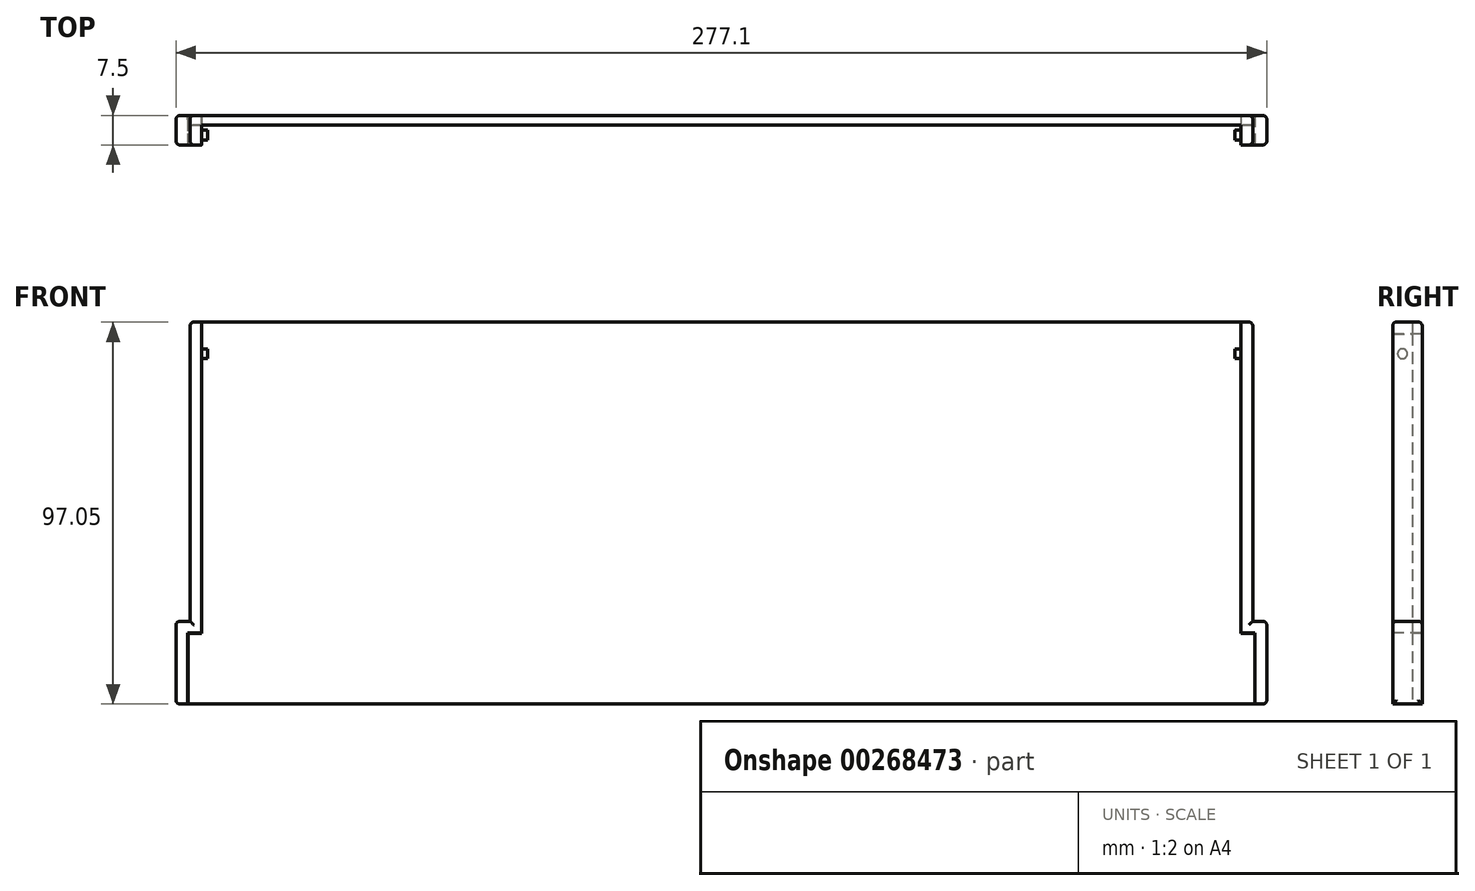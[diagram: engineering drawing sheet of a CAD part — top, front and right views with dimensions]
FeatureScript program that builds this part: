
annotation { "Feature Type Name" : "Feature", "Feature Type Description" : "" }
export const myFeature = defineFeature(function(context is Context, id is Id, definition is map)
    precondition{}
    {
        {
            var Q0;
            Q0=qCreatedBy(makeId("Front.planeOp"),FACE);
            var sketch = newSketch(context, id + "F0", { "sketchPlane" : qUnion([Q0])});
            skLineSegment(sketch, "E0", {"start": v(0, 0) * mm, "end": v(-135.5, 0) * mm});
            skLineSegment(sketch, "E1", {"start": v(-135.5, 0) * mm, "end": v(-135.5, 18) * mm});
            skLineSegment(sketch, "E2", {"start": v(-135.5, 18) * mm, "end": v(-132, 18) * mm});
            skLineSegment(sketch, "E3", {"start": v(-132, 18) * mm, "end": v(-132, 160) * mm});
            skLineSegment(sketch, "E4", {"start": v(-132, 160) * mm, "end": v(132, 160) * mm});
            skLineSegment(sketch, "E5", {"start": v(132, 160) * mm, "end": v(132, 18) * mm});
            skLineSegment(sketch, "E6", {"start": v(132, 18) * mm, "end": v(135.5, 18) * mm});
            skLineSegment(sketch, "E7", {"start": v(135.5, 18) * mm, "end": v(135.5, 0) * mm});
            skLineSegment(sketch, "E8", {"start": v(135.5, 0) * mm, "end": v(0, 0) * mm});
            skSolve(sketch);
        }
        {
            var Q0;
            Q0=makeQuery(id+"F0.imprint","IMPRINT",FACE,{"disambiguationData":[TD([[makeQuery(id+"F0.imprint","IMPRINT",EDGE,{"derivedFrom":sQuery(id+"F0.wireOp",EDGE,"E0")}),-1.0]])]});
            extrude(context, id + "F1", {"entities" : qUnion([Q0]), "oppositeDirection" : true, "depth" : 5 * mm, "offsetDistance" : 25 * mm});
        }
        {
            var Q0;
            Q0=makeQuery(id+"F1.opExtrude","CAP_FACE",FACE,{"disambiguationData":[OSD([sQuery(id+"F0.wireOp",EDGE,"E0"),sQuery(id+"F0.wireOp",EDGE,"E1"),sQuery(id+"F0.wireOp",EDGE,"E2"),sQuery(id+"F0.wireOp",EDGE,"E3"),sQuery(id+"F0.wireOp",EDGE,"E4"),sQuery(id+"F0.wireOp",EDGE,"E5"),sQuery(id+"F0.wireOp",EDGE,"E6"),sQuery(id+"F0.wireOp",EDGE,"E7"),sQuery(id+"F0.wireOp",EDGE,"E8")])],"isStart":true});
            var sketch = newSketch(context, id + "F2", { "sketchPlane" : qUnion([Q0])});
            skLineSegment(sketch, "E9", {"start": v(-135.55, 0) * mm, "end": v(-135.55, 18.05) * mm});
            skLineSegment(sketch, "E10", {"start": v(-135.55, 18.05) * mm, "end": v(-132.05, 18.05) * mm});
            skLineSegment(sketch, "E11", {"start": v(-132.05, 18.05) * mm, "end": v(-132.05, 94.05) * mm});
            skLineSegment(sketch, "E12", {"start": v(-132.05, 94.05) * mm, "end": v(132.05, 94.05) * mm});
            skLineSegment(sketch, "E13", {"start": v(132.05, 94.05) * mm, "end": v(132.05, 18.05) * mm});
            skLineSegment(sketch, "E14", {"start": v(132.05, 18.05) * mm, "end": v(135.55, 18.05) * mm});
            skLineSegment(sketch, "E15", {"start": v(135.55, 18.05) * mm, "end": v(135.55, 0) * mm});
            skLineSegment(sketch, "E16", {"start": v(135.55, 0) * mm, "end": v(138.55, 0) * mm});
            skLineSegment(sketch, "E17", {"start": v(138.55, 0) * mm, "end": v(138.55, 21.05) * mm});
            skLineSegment(sketch, "E18", {"start": v(138.55, 21.05) * mm, "end": v(135, 21.05) * mm});
            skLineSegment(sketch, "E19", {"start": v(135, 21.05) * mm, "end": v(135, 97.05) * mm});
            skLineSegment(sketch, "E20", {"start": v(135, 97.05) * mm, "end": v(-135, 97.05) * mm});
            skLineSegment(sketch, "E21", {"start": v(-135, 97.05) * mm, "end": v(-135, 21.05) * mm});
            skLineSegment(sketch, "E22", {"start": v(-135, 21.05) * mm, "end": v(-138.55, 21.05) * mm});
            skLineSegment(sketch, "E23", {"start": v(-138.55, 21.05) * mm, "end": v(-138.55, 0) * mm});
            skLineSegment(sketch, "E24", {"start": v(-138.55, 0) * mm, "end": v(-135.55, 0) * mm});
            skLineSegment(sketch, "E25.bottom", {"start": v(138.55, 0) * mm, "end": v(135.55, 0) * mm});
            skLineSegment(sketch, "E25.top", {"start": v(138.55, 0) * mm, "end": v(135.55, 0) * mm});
            skLineSegment(sketch, "E25.left", {"start": v(138.55, 0) * mm, "end": v(138.55, 0) * mm});
            skLineSegment(sketch, "E25.right", {"start": v(135.55, 0) * mm, "end": v(135.55, 0) * mm});
            skLineSegment(sketch, "E26.left", {"start": v(-138.55, 0) * mm, "end": v(-138.55, 0) * mm});
            skLineSegment(sketch, "E26.right", {"start": v(-135.55, 0) * mm, "end": v(-135.55, 0) * mm});
            skSolve(sketch);
        }
        {
            var Q0;
            Q0=makeQuery(id+"F1.opExtrude","SWEPT_FACE",FACE,{"disambiguationData":[OSD([sQuery(id+"F0.wireOp",EDGE,"E5")])]});
            var sketch = newSketch(context, id + "F3", { "sketchPlane" : qUnion([Q0])});
            skCircle(sketch, "E27", {"center": v(2.5, 89) * mm, "radius": 1.25 * mm});
            skPoint(sketch, "E27.centerSnap0", {"position": v(5, 89) * mm});
            skSolve(sketch);
        }
        {
            var Q0;
            Q0=makeQuery(id+"F1.opExtrude","SWEPT_FACE",FACE,{"disambiguationData":[OSD([sQuery(id+"F0.wireOp",EDGE,"E3")])]});
            var sketch = newSketch(context, id + "F4", { "sketchPlane" : qUnion([Q0])});
            skCircle(sketch, "E28", {"center": v(-2.5, 89) * mm, "radius": 1.25 * mm});
            skPoint(sketch, "E28.centerSnap0", {"position": v(-5, 89) * mm});
            skSolve(sketch);
        }
        {
            var Q0;
            Q0 = qSketchRegion(id + "F2", true);
            extrude(context, id + "F5", {"entities" : qUnion([Q0]), "operationType" : NewBodyOperationType.ADD, "oppositeDirection" : true, "depth" : 7.5 * mm, "offsetDistance" : 25 * mm});
        }
        {
            var Q0;
            {var subQ0=sQuery(id+"F0.wireOp",EDGE,"E3");var subQ1=sQuery(id+"F0.wireOp",EDGE,"E2");var subQ2=sQuery(id+"F0.wireOp",EDGE,"E1");var subQ3=sQuery(id+"F0.wireOp",EDGE,"E8");var subQ4=sQuery(id+"F0.wireOp",EDGE,"E0");var subQ5=sQuery(id+"F0.wireOp",EDGE,"E5");var subQ6=sQuery(id+"F0.wireOp",EDGE,"E6");var subQ7=sQuery(id+"F0.wireOp",EDGE,"E7");Q0=makeQuery(id+"F5.boolean.opBoolean","SPLIT",FACE,{"disambiguationData":[TD([makeQuery(id+"F1.opExtrude","SWEPT_FACE",FACE,{"disambiguationData":[OSD([subQ2])]})])],"derivedFrom":makeQuery(id+"F1.opExtrude","CAP_FACE",FACE,{"disambiguationData":[OSD([subQ4,subQ2,subQ1,subQ0,sQuery(id+"F0.wireOp",EDGE,"E4"),subQ5,subQ6,subQ7,subQ3])],"isStart":false})});}
            extrude(context, id + "F6", {"entities" : qUnion([Q0]), "operationType" : NewBodyOperationType.ADD, "depth" : 2.5 * mm, "offsetDistance" : 25 * mm});
        }
        {
            var Q0;
            Q0 = qSketchRegion(id + "F0", true);
            extrude(context, id + "F7", {"entities" : qUnion([Q0]), "operationType" : NewBodyOperationType.REMOVE, "oppositeDirection" : true, "depth" : 5 * mm, "offsetDistance" : 25 * mm});
        }
        {
            var Q0;
            Q0 = qSketchRegion(id + "F3", true);
            var Q1;
            Q1 = qSketchRegion(id + "F4", true);
            extrude(context, id + "F8", {"entities" : qUnion([Q0, Q1]), "operationType" : NewBodyOperationType.ADD, "depth" : 1.5 * mm, "offsetDistance" : 25 * mm});
        }
        {
            var Q0;
            Q0 = qSketchRegion(id + "F3", true);
            var Q1;
            Q1 = qSketchRegion(id + "F4", true);
            extrude(context, id + "F9", {"entities" : qUnion([Q0, Q1]), "operationType" : NewBodyOperationType.ADD, "oppositeDirection" : true, "depth" : 1.5 * mm, "offsetDistance" : 25 * mm});
        }
        {
            var Q0;
            Q0=makeQuery(id+"F5.opExtrude","CAP_EDGE",EDGE,{"disambiguationData":[OSD([sQuery(id+"F2.wireOp",EDGE,"E21")])],"isStart":true});
            var Q1;
            Q1=makeQuery(id+"F5.opExtrude","CAP_EDGE",EDGE,{"disambiguationData":[OSD([sQuery(id+"F2.wireOp",EDGE,"E21")])],"isStart":false});
            var Q2;
            Q2=makeQuery(id+"F5.opExtrude","CAP_EDGE",EDGE,{"disambiguationData":[OSD([sQuery(id+"F2.wireOp",EDGE,"E19")])],"isStart":false});
            var Q3;
            Q3=makeQuery(id+"F5.opExtrude","CAP_EDGE",EDGE,{"disambiguationData":[OSD([sQuery(id+"F2.wireOp",EDGE,"E19")])],"isStart":true});
            var Q4;
            Q4=makeQuery(id+"F5.opExtrude","SWEPT_EDGE",EDGE,{"disambiguationData":[OSD([sQuery(id+"F2.wireOp",EDGE,"E19"),sQuery(id+"F2.wireOp",EDGE,"E20")])]});
            var Q5;
            Q5=makeQuery(id+"F5.opExtrude","CAP_EDGE",EDGE,{"disambiguationData":[OSD([sQuery(id+"F2.wireOp",EDGE,"E20")])],"isStart":false});
            var Q6;
            Q6=makeQuery(id+"F5.opExtrude","SWEPT_EDGE",EDGE,{"disambiguationData":[OSD([sQuery(id+"F2.wireOp",EDGE,"E20"),sQuery(id+"F2.wireOp",EDGE,"E21")])]});
            var Q7;
            Q7=makeQuery(id+"F5.opExtrude","CAP_EDGE",EDGE,{"disambiguationData":[OSD([sQuery(id+"F2.wireOp",EDGE,"E22")])],"isStart":true});
            var Q8;
            Q8=makeQuery(id+"F5.opExtrude","CAP_EDGE",EDGE,{"disambiguationData":[OSD([sQuery(id+"F2.wireOp",EDGE,"E22")])],"isStart":false});
            var Q9;
            Q9=makeQuery(id+"F5.opExtrude","SWEPT_EDGE",EDGE,{"disambiguationData":[OSD([sQuery(id+"F2.wireOp",EDGE,"E22"),sQuery(id+"F2.wireOp",EDGE,"E23")])]});
            var Q10;
            Q10=makeQuery(id+"F5.opExtrude","CAP_EDGE",EDGE,{"disambiguationData":[OSD([sQuery(id+"F2.wireOp",EDGE,"E23")])],"isStart":true});
            var Q11;
            Q11=makeQuery(id+"F5.opExtrude","CAP_EDGE",EDGE,{"disambiguationData":[OSD([sQuery(id+"F2.wireOp",EDGE,"E23")])],"isStart":false});
            var Q12;
            Q12=makeQuery(id+"F5.opExtrude","SWEPT_EDGE",EDGE,{"disambiguationData":[OSD([sQuery(id+"F2.wireOp",EDGE,"E23"),sQuery(id+"F2.wireOp",EDGE,"E24")])]});
            var Q13;
            Q13=makeQuery(id+"F6.opExtrude","CAP_EDGE",EDGE,{"disambiguationData":[OSD([sQuery(id+"F0.wireOp",EDGE,"E0"),sQuery(id+"F0.wireOp",EDGE,"E8")])],"isStart":false});
            var Q14;
            Q14=makeQuery(id+"F5.opExtrude","CAP_EDGE",EDGE,{"disambiguationData":[OSD([sQuery(id+"F2.wireOp",EDGE,"E24")])],"isStart":false});
            var Q15;
            Q15=makeQuery(id+"F5.opExtrude","CAP_EDGE",EDGE,{"disambiguationData":[OSD([sQuery(id+"F2.wireOp",EDGE,"E25.top")])],"isStart":false});
            var Q16;
            Q16=makeQuery(id+"F5.opExtrude","CAP_EDGE",EDGE,{"disambiguationData":[OSD([sQuery(id+"F2.wireOp",EDGE,"E17")])],"isStart":false});
            var Q17;
            Q17=makeQuery(id+"F5.opExtrude","SWEPT_EDGE",EDGE,{"disambiguationData":[OSD([sQuery(id+"F2.wireOp",EDGE,"E17"),sQuery(id+"F2.wireOp",EDGE,"E25.top")])]});
            var Q18;
            Q18=makeQuery(id+"F5.opExtrude","CAP_EDGE",EDGE,{"disambiguationData":[OSD([sQuery(id+"F2.wireOp",EDGE,"E17")])],"isStart":true});
            var Q19;
            Q19=makeQuery(id+"F5.opExtrude","SWEPT_EDGE",EDGE,{"disambiguationData":[OSD([sQuery(id+"F2.wireOp",EDGE,"E17"),sQuery(id+"F2.wireOp",EDGE,"E18")])]});
            var Q20;
            Q20=makeQuery(id+"F5.opExtrude","CAP_EDGE",EDGE,{"disambiguationData":[OSD([sQuery(id+"F2.wireOp",EDGE,"E18")])],"isStart":true});
            var Q21;
            Q21=makeQuery(id+"F5.opExtrude","CAP_EDGE",EDGE,{"disambiguationData":[OSD([sQuery(id+"F2.wireOp",EDGE,"E18")])],"isStart":false});
            var Q22;
            {var subQ1=sQuery(id+"F0.wireOp",EDGE,"E5");var subQ2=sQuery(id+"F2.wireOp",EDGE,"E20");Q22=makeQuery(id+"F5.boolean.opBoolean","SPLIT",EDGE,{"disambiguationData":[TD([makeQuery(id+"F1.opExtrude","SWEPT_FACE",FACE,{"disambiguationData":[OSD([subQ1])]})])],"derivedFrom":makeQuery(id+"F5.opExtrude","CAP_EDGE",EDGE,{"disambiguationData":[OSD([subQ2])],"isStart":true})});}
            var Q23;
            {var subQ0=sQuery(id+"F2.wireOp",EDGE,"E20");var subQ2=sQuery(id+"F0.wireOp",EDGE,"E3");Q23=makeQuery(id+"F5.boolean.opBoolean","SPLIT",EDGE,{"disambiguationData":[TD([makeQuery(id+"F1.opExtrude","SWEPT_FACE",FACE,{"disambiguationData":[OSD([subQ2])]})])],"derivedFrom":makeQuery(id+"F5.opExtrude","CAP_EDGE",EDGE,{"disambiguationData":[OSD([subQ0])],"isStart":true})});}
            fillet(context, id + "F10", {"entities" : qUnion([Q0, Q1, Q2, Q3, Q4, Q5, Q6, Q7, Q8, Q9, Q10, Q11, Q12, Q13, Q14, Q15, Q16, Q17, Q18, Q19, Q20, Q21, Q22, Q23]), "radius" : 1 * mm, "tangentPropagation" : true, "allowEdgeOverflow" : false});
        }
    });
